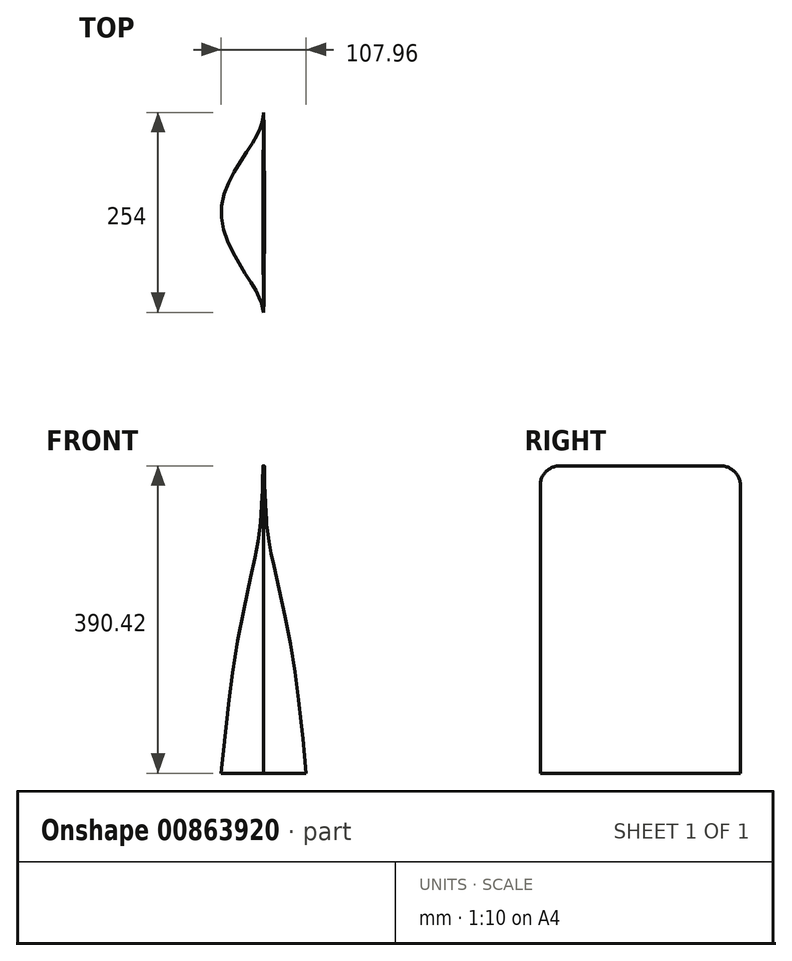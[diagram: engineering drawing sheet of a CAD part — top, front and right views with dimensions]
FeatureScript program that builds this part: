
annotation { "Feature Type Name" : "Feature", "Feature Type Description" : "" }
export const myFeature = defineFeature(function(context is Context, id is Id, definition is map)
    precondition{}
    {
        {
            var Q0;
            Q0=qCreatedBy(makeId("Top.planeOp"),FACE);
            var sketch = newSketch(context, id + "F0", { "sketchPlane" : qUnion([Q0])});
            skFitSpline(sketch, "E0", {"points": [v(0, 127) * mm, v(-8.28, 98.29) * mm, v(-53.98, 0) * mm, v(-8.95, -101) * mm, v(0, -127) * mm], "startDerivative": vector(-16.8, -142.22) * mm, "endDerivative": vector(29.76, -118.73) * mm});
            skFitSpline(sketch, "E1.MirrorCS", {"points": [v(0, 127) * mm, v(8.28, 98.29) * mm, v(53.98, 0) * mm, v(8.95, -101) * mm, v(0, -127) * mm], "startDerivative": vector(16.8, -142.22) * mm, "endDerivative": vector(-29.76, -118.73) * mm});
            skSolve(sketch);
        }
        {
            var Q0;
            Q0=qCreatedBy(makeId("Top.planeOp"),FACE);
            cPlane(context, id + "F1", {"entities" : qUnion([Q0]), "cplaneType" : CPlaneType.OFFSET, "offset" : 312.52 * mm, "width" : 152.4 * mm, "height" : 152.4 * mm});
        }
        {
            var Q0;
            Q0=qCreatedBy(id+"F1.planeOp",FACE);
            var sketch = newSketch(context, id + "F2", { "sketchPlane" : qUnion([Q0])});
            skFitSpline(sketch, "E2", {"points": [v(0, 127) * mm, v(-1.96, 98.87) * mm, v(-4.78, 0) * mm, v(-2.62, -100.36) * mm, v(0, -127) * mm], "startDerivative": vector(-5.36, -137.22) * mm, "endDerivative": vector(10.77, -131.52) * mm});
            skFitSpline(sketch, "E3.MirrorCS", {"points": [v(0, 127) * mm, v(1.96, 98.87) * mm, v(4.19, 0) * mm, v(2.62, -100.36) * mm, v(0, -127) * mm], "startDerivative": vector(5.36, -137.22) * mm, "endDerivative": vector(-10.77, -131.52) * mm});
            skSolve(sketch);
        }
        {
            var Q0;
            Q0=qCreatedBy(makeId("Top.planeOp"),FACE);
            cPlane(context, id + "F3", {"entities" : qUnion([Q0]), "cplaneType" : CPlaneType.OFFSET, "offset" : 390.65 * mm, "width" : 152.4 * mm, "height" : 152.4 * mm});
        }
        {
            var Q0;
            Q0=qCreatedBy(id+"F3.planeOp",FACE);
            var sketch = newSketch(context, id + "F4", { "sketchPlane" : qUnion([Q0])});
            skPoint(sketch, "E4.1.end.orphan", {"position": v(0, -127) * mm});
            skPoint(sketch, "E4.1.start.orphan", {"position": v(0, 127) * mm});
            skPoint(sketch, "E4.0.end.orphan", {"position": v(0, -127) * mm});
            skPoint(sketch, "E4.0.start.orphan", {"position": v(0, 127) * mm});
            skFitSpline(sketch, "E5", {"points": [v(0, 127) * mm, v(-0.95, 0) * mm, v(0, -127) * mm], "startDerivative": vector(-2.84, -254) * mm, "endDerivative": vector(2.84, -254) * mm});
            skFitSpline(sketch, "E6.MirrorCS", {"points": [v(0, 127) * mm, v(0.95, 0) * mm, v(0, -127) * mm], "startDerivative": vector(2.84, -254) * mm, "endDerivative": vector(-2.84, -254) * mm});
            skSolve(sketch);
        }
        {
            var Q0;
            Q0=qCreatedBy(makeId("Top.planeOp"),FACE);
            cPlane(context, id + "F5", {"entities" : qUnion([Q0]), "cplaneType" : CPlaneType.OFFSET, "offset" : 205.16 * mm, "width" : 152.4 * mm, "height" : 152.4 * mm});
        }
        {
            var Q0;
            Q0=qCreatedBy(id+"F5.planeOp",FACE);
            var sketch = newSketch(context, id + "F6", { "sketchPlane" : qUnion([Q0])});
            skFitSpline(sketch, "E7", {"points": [v(0, 127) * mm, v(-4.94, 97.33) * mm, v(-26, 0) * mm, v(-5.73, -100.66) * mm, v(0, -127) * mm], "startDerivative": vector(-13.33, -143.49) * mm, "endDerivative": vector(21.74, -130.25) * mm});
            skFitSpline(sketch, "E8.MirrorCS", {"points": [v(0, 127) * mm, v(4.94, 97.33) * mm, v(26, 0) * mm, v(5.73, -100.66) * mm, v(0, -127) * mm], "startDerivative": vector(13.33, -143.49) * mm, "endDerivative": vector(-21.74, -130.25) * mm});
            skSolve(sketch);
        }
        {
            var Q0;
            Q0=makeQuery(id+"F0.imprint","IMPRINT",FACE,{"disambiguationData":[TD([[makeQuery(id+"F0.imprint","IMPRINT",EDGE,{"derivedFrom":sQuery(id+"F0.wireOp",EDGE,"E0")}),1.0]])]});
            var Q1;
            Q1=makeQuery(id+"F6.imprint","IMPRINT",FACE,{"disambiguationData":[TD([[makeQuery(id+"F6.imprint","IMPRINT",EDGE,{"derivedFrom":sQuery(id+"F6.wireOp",EDGE,"E7")}),1.0]])]});
            var Q2;
            Q2=makeQuery(id+"F2.imprint","IMPRINT",FACE,{"disambiguationData":[TD([[makeQuery(id+"F2.imprint","IMPRINT",EDGE,{"derivedFrom":sQuery(id+"F2.wireOp",EDGE,"E2")}),1.0]])]});
            var Q3;
            Q3=makeQuery(id+"F4.imprint","IMPRINT",FACE,{"disambiguationData":[TD([[makeQuery(id+"F4.imprint","IMPRINT",EDGE,{"derivedFrom":sQuery(id+"F4.wireOp",EDGE,"E5")}),1.0]])]});
            loft(context, id + "F7", {"sheetProfilesArray" : [{ "sheetProfileEntities" : qUnion([Q0]) }, { "sheetProfileEntities" : qUnion([Q1]) }, { "sheetProfileEntities" : qUnion([Q2]) }, { "sheetProfileEntities" : qUnion([Q3]) }]});
        }
        {
            var Q0;
            Q0=qCreatedBy(makeId("Right.planeOp"),FACE);
            var sketch = newSketch(context, id + "F8", { "sketchPlane" : qUnion([Q0])});
            skLineSegment(sketch, "E9", {"start": v(101.86, 390.42) * mm, "end": v(-101.86, 390.42) * mm});
            skLineSegment(sketch, "E10", {"start": v(127.26, 365.02) * mm, "end": v(127.26, 323.06) * mm});
            skLineSegment(sketch, "E11", {"start": v(-127.26, 365.02) * mm, "end": v(-127.26, 336.26) * mm});
            skLineSegment(sketch, "E12", {"start": v(-127.26, 336.26) * mm, "end": v(-183.65, 336.26) * mm});
            skLineSegment(sketch, "E13", {"start": v(-183.65, 336.26) * mm, "end": v(-183.65, 449.6) * mm});
            skLineSegment(sketch, "E14", {"start": v(-183.65, 449.6) * mm, "end": v(198.7, 449.6) * mm});
            skLineSegment(sketch, "E15", {"start": v(198.7, 449.6) * mm, "end": v(198.7, 322.78) * mm});
            skLineSegment(sketch, "E16", {"start": v(198.7, 322.78) * mm, "end": v(127.26, 323.06) * mm});
            skPoint(sketch, "E17.visualSharp", {"position": v(127.26, 390.42) * mm});
            skArc(sketch, "E17.filletArc", {"start": v(127.26, 365.02) * mm, "mid": v(119.82, 382.98) * mm, "end": v(101.86, 390.42) * mm});
            skPoint(sketch, "E18.visualSharp", {"position": v(-127.26, 390.42) * mm});
            skArc(sketch, "E18.filletArc", {"start": v(-101.86, 390.42) * mm, "mid": v(-119.82, 382.98) * mm, "end": v(-127.26, 365.02) * mm});
            skSolve(sketch);
        }
        {
            var Q0;
            Q0=makeQuery(id+"F8.imprint","IMPRINT",FACE,{"disambiguationData":[TD([[makeQuery(id+"F8.imprint","IMPRINT",EDGE,{"derivedFrom":sQuery(id+"F8.wireOp",EDGE,"E9")}),-1.0]])]});
            extrude(context, id + "F9", {"entities" : qUnion([Q0]), "operationType" : NewBodyOperationType.REMOVE, "endBound" : BoundingType.SYMMETRIC, "oppositeDirection" : true, "depth" : 25.4 * mm, "offsetDistance" : 25.4 * mm});
        }
    });
